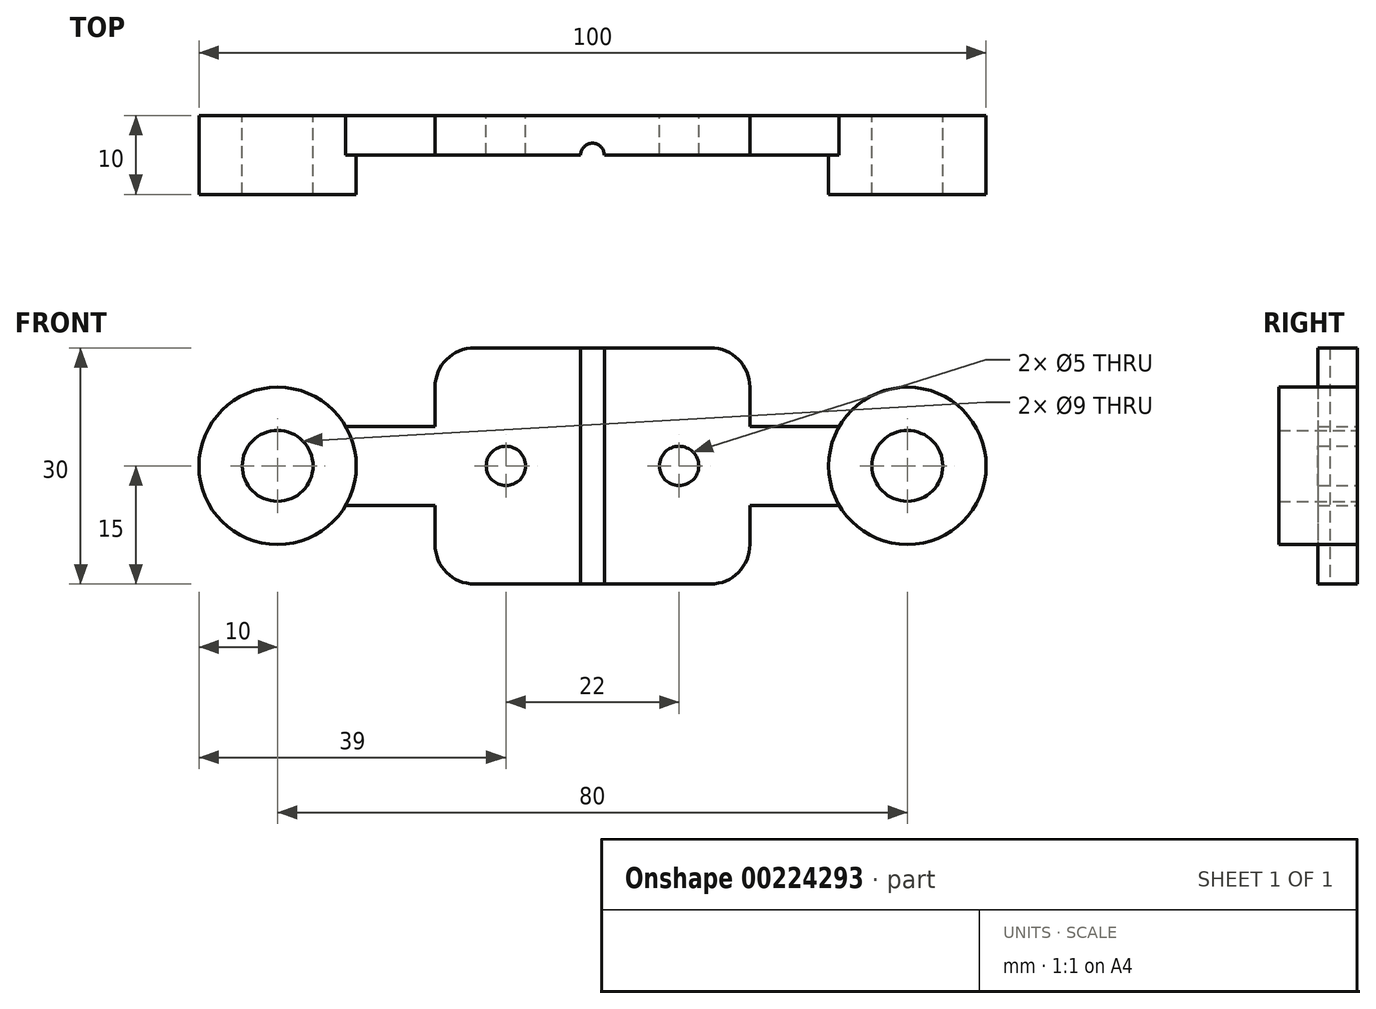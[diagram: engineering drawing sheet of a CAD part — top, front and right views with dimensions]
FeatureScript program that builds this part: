
annotation { "Feature Type Name" : "Feature", "Feature Type Description" : "" }
export const myFeature = defineFeature(function(context is Context, id is Id, definition is map)
    precondition{}
    {
        {
            var Q0;
            Q0=qCreatedBy(makeId("Front.planeOp"),FACE);
            var sketch = newSketch(context, id + "F0", { "sketchPlane" : qUnion([Q0])});
            skLineSegment(sketch, "E0.bottom", {"start": v(-20, 15) * mm, "end": v(20, 15) * mm});
            skLineSegment(sketch, "E0.top", {"start": v(-20, -15) * mm, "end": v(20, -15) * mm});
            skLineSegment(sketch, "E0.left", {"start": v(-20, 15) * mm, "end": v(-20, -15) * mm});
            skLineSegment(sketch, "E0.right", {"start": v(20, 15) * mm, "end": v(20, -15) * mm});
            skPoint(sketch, "E0.middle", {"position": v(0, 0) * mm});
            skLineSegment(sketch, "E1.bottom", {"start": v(-20, 5) * mm, "end": v(-35, 5) * mm});
            skLineSegment(sketch, "E1.top", {"start": v(-20, -5) * mm, "end": v(-35, -5) * mm});
            skLineSegment(sketch, "E1.left", {"start": v(-20, 5) * mm, "end": v(-20, -5) * mm});
            skLineSegment(sketch, "E1.right", {"start": v(-35, 5) * mm, "end": v(-35, -5) * mm});
            skLineSegment(sketch, "E2.bottom", {"start": v(20, 5) * mm, "end": v(35, 5) * mm});
            skLineSegment(sketch, "E2.top", {"start": v(20, -5) * mm, "end": v(35, -5) * mm});
            skLineSegment(sketch, "E2.left", {"start": v(20, 5) * mm, "end": v(20, -5) * mm});
            skLineSegment(sketch, "E2.right", {"start": v(35, 5) * mm, "end": v(35, -5) * mm});
            skCircle(sketch, "E3", {"center": v(11, 0) * mm, "radius": 2.5 * mm});
            skCircle(sketch, "E4", {"center": v(-11, 0) * mm, "radius": 2.5 * mm});
            skSolve(sketch);
        }
        {
            var Q0;
            Q0=makeQuery(id+"F0.imprint","IMPRINT",FACE,{"disambiguationData":[TD([[makeQuery(id+"F0.imprint","IMPRINT",EDGE,{"derivedFrom":sQuery(id+"F0.wireOp",EDGE,"E1.bottom")}),1.0]])]});
            var Q1;
            {var subQ3=sQuery(id+"F0.wireOp",EDGE,"E0.bottom");Q1=makeQuery(id+"F0.imprint","IMPRINT",FACE,{"disambiguationData":[TD([[makeQuery(id+"F0.imprint","IMPRINT",EDGE,{"derivedFrom":subQ3}),-1.0]])]});}
            var Q2;
            Q2=makeQuery(id+"F0.imprint","IMPRINT",FACE,{"disambiguationData":[TD([[makeQuery(id+"F0.imprint","IMPRINT",EDGE,{"derivedFrom":sQuery(id+"F0.wireOp",EDGE,"E2.bottom")}),-1.0]])]});
            extrude(context, id + "F1", {"entities" : qUnion([Q0, Q1, Q2]), "depth" : 5 * mm});
        }
        {
            var Q0;
            Q0=makeQuery(id+"F1.opExtrude","SWEPT_FACE",FACE,{"disambiguationData":[OSD([sQuery(id+"F0.wireOp",EDGE,"E0.top")])]});
            var sketch = newSketch(context, id + "F2", { "sketchPlane" : qUnion([Q0])});
            skCircle(sketch, "E5", {"center": v(0, 5) * mm, "radius": 1.5 * mm});
            skSolve(sketch);
        }
        {
            var Q0;
            {var subQ0=sQuery(id+"F2.wireOp",EDGE,"8NvyphFo-orXO-u74B-SdUR-tZl27edXpFAf");var subQ1=makeQuery(id+"F1.opExtrude","CAP_EDGE",EDGE,{"disambiguationData":[OSD([sQuery(id+"F0.wireOp",EDGE,"E0.top")])],"isStart":true});var subQ2=makeQuery(id+"F2.imprint","INTERSECT",VERTEX,{"disambiguationData":[OD(0.0)],"derivedFrom":[subQ1,subQ0]});Q0=makeQuery(id+"F2.imprint","IMPRINT",FACE,{"disambiguationData":[TD([[makeQuery(id+"F2.imprint","IMPRINT",EDGE,{"disambiguationData":[TD([[subQ2,1.0]])],"derivedFrom":subQ0}),1.0]])]});}
            var Q1;
            {var subQ0=sQuery(id+"F2.wireOp",EDGE,"E5");var subQ1=makeQuery(id+"F1.opExtrude","CAP_EDGE",EDGE,{"disambiguationData":[OSD([sQuery(id+"F0.wireOp",EDGE,"E0.top")])],"isStart":false});var subQ2=makeQuery(id+"F2.imprint","INTERSECT",VERTEX,{"disambiguationData":[OD(0.0)],"derivedFrom":[subQ1,subQ0]});Q1=makeQuery(id+"F2.imprint","IMPRINT",FACE,{"disambiguationData":[TD([[makeQuery(id+"F2.imprint","IMPRINT",EDGE,{"disambiguationData":[TD([[subQ2,-1.0]])],"derivedFrom":subQ0}),1.0]])]});}
            extrude(context, id + "F3", {"entities" : qUnion([Q0, Q1]), "operationType" : NewBodyOperationType.REMOVE, "oppositeDirection" : true, "depth" : 31 * mm});
        }
        {
            var Q0;
            {var subQ0=sQuery(id+"F0.wireOp",EDGE,"E0.right");var subQ1=sQuery(id+"F0.wireOp",EDGE,"E0.top");var subQ3=sQuery(id+"F0.wireOp",EDGE,"E2.top");var subQ4=sQuery(id+"F0.wireOp",EDGE,"E3");var subQ5=sQuery(id+"F0.wireOp",EDGE,"E0.bottom");var subQ6=sQuery(id+"F0.wireOp",EDGE,"E2.bottom");var subQ7=sQuery(id+"F0.wireOp",EDGE,"E2.right");Q0=makeQuery(id+"F3.boolean.opBoolean","SPLIT",FACE,{"disambiguationData":[TD([makeQuery(id+"F1.opExtrude","SWEPT_FACE",FACE,{"disambiguationData":[OSD([subQ6])]})])],"derivedFrom":makeQuery(id+"F1.opExtrude","CAP_FACE",FACE,{"disambiguationData":[OSD([subQ5,subQ1,sQuery(id+"F0.wireOp",EDGE,"E0.left"),subQ0,sQuery(id+"F0.wireOp",EDGE,"E1.bottom"),sQuery(id+"F0.wireOp",EDGE,"E1.top"),sQuery(id+"F0.wireOp",EDGE,"E1.right"),subQ6,subQ3,subQ7,subQ4,sQuery(id+"F0.wireOp",EDGE,"E4")])],"isStart":true})});}
            var sketch = newSketch(context, id + "F4", { "sketchPlane" : qUnion([Q0])});
            skCircle(sketch, "E6", {"center": v(-40, 0) * mm, "radius": 10 * mm});
            skCircle(sketch, "E7", {"center": v(-40, 0) * mm, "radius": 4.5 * mm});
            skCircle(sketch, "E8", {"center": v(40, 0) * mm, "radius": 4.5 * mm});
            skCircle(sketch, "E9", {"center": v(40, 0) * mm, "radius": 10 * mm});
            skSolve(sketch);
        }
        {
            var Q0;
            Q0=makeQuery(id+"F4.imprint","IMPRINT",FACE,{"disambiguationData":[TD([[makeQuery(id+"F4.imprint","IMPRINT",EDGE,{"derivedFrom":sQuery(id+"F4.wireOp",EDGE,"E8")}),-1.0]])]});
            var Q1;
            Q1=makeQuery(id+"F4.imprint","IMPRINT",FACE,{"disambiguationData":[TD([[makeQuery(id+"F4.imprint","IMPRINT",EDGE,{"derivedFrom":sQuery(id+"F4.wireOp",EDGE,"E7")}),-1.0]])]});
            var Q2;
            {var subQ5=makeQuery(id+"F1.opExtrude","CAP_EDGE",EDGE,{"disambiguationData":[OSD([sQuery(id+"F0.wireOp",EDGE,"E2.right")])],"isStart":true});Q2=makeQuery(id+"F4.imprint","IMPRINT",FACE,{"disambiguationData":[TD([[makeQuery(id+"F4.imprint","IMPRINT",EDGE,{"derivedFrom":subQ5}),1.0]])]});}
            var Q3;
            {var subQ5=makeQuery(id+"F1.opExtrude","CAP_EDGE",EDGE,{"disambiguationData":[OSD([sQuery(id+"F0.wireOp",EDGE,"E1.right")])],"isStart":true});Q3=makeQuery(id+"F4.imprint","IMPRINT",FACE,{"disambiguationData":[TD([[makeQuery(id+"F4.imprint","IMPRINT",EDGE,{"derivedFrom":subQ5}),-1.0]])]});}
            extrude(context, id + "F5", {"entities" : qUnion([Q0, Q1, Q2, Q3]), "operationType" : NewBodyOperationType.ADD, "oppositeDirection" : true, "depth" : 10 * mm});
        }
        {
            var Q0;
            Q0=makeQuery(id+"F1.opExtrude","SWEPT_EDGE",EDGE,{"disambiguationData":[OSD([sQuery(id+"F0.wireOp",EDGE,"E0.top"),sQuery(id+"F0.wireOp",EDGE,"E0.right")])]});
            var Q1;
            Q1=makeQuery(id+"F1.opExtrude","SWEPT_EDGE",EDGE,{"disambiguationData":[OSD([sQuery(id+"F0.wireOp",EDGE,"E0.bottom"),sQuery(id+"F0.wireOp",EDGE,"E0.right")])]});
            var Q2;
            Q2=makeQuery(id+"F1.opExtrude","SWEPT_EDGE",EDGE,{"disambiguationData":[OSD([sQuery(id+"F0.wireOp",EDGE,"E0.bottom"),sQuery(id+"F0.wireOp",EDGE,"E0.left")])]});
            var Q3;
            Q3=makeQuery(id+"F1.opExtrude","SWEPT_EDGE",EDGE,{"disambiguationData":[OSD([sQuery(id+"F0.wireOp",EDGE,"E0.top"),sQuery(id+"F0.wireOp",EDGE,"E0.left")])]});
            fillet(context, id + "F6", {"entities" : qUnion([Q0, Q1, Q2, Q3]), "radius" : 5 * mm, "tangentPropagation" : true, "allowEdgeOverflow" : false});
        }
    });
